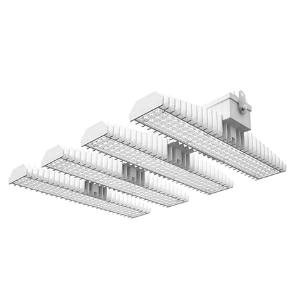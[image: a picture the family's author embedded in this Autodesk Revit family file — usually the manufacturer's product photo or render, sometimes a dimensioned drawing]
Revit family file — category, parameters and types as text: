
# Revit family: 3f_filippi_-_3f_lem_medio_3f_filippi_-_58895_a0811_-_3f_lem_4_led_200_cr_medio___vt_021e
name_source: partatom
category: Lighting Fixtures
units: mm (PartAtom-declared; Revit-internal decimal feet)

## family parameters
Cut with Voids When Loaded = No
Host = Face
Light Source = No
Part Type = Normal
Room Calculation Point = No
Round Connector Dimension = Use Diameter
Shared = No

## types (1)
- 3F Filippi - 3F LEM Medio (1 x LED, 30958 lm, 218 W, 4000 K)
    Apparent Load = 218 VA
    Approval mark = CE
    CIE Flux Codes = 83 96 99 100 100
    Color Rendering = 80
    Color Temperature = 4000 K
    Control Gear = Electronic ballast
    Default Elevation = 1800 mm
    Description = Industrial luminaire with high light output and high luminous efficiency designed with the most innovative technologies for environments with temperature up to 55°C.

ILLUMINOTECHNICAL
Luminous efficiency 100% (DLOR 99%, ULOR 1%).
Initial luminous flux of the luminaire 30958 lm.
Medium distribution with rectangular shape.
Installation Interdistance Transv.D = 1.02 x hu - Long.D = 1.06 x hu.
Tabular UGR (CIE 117 - 4H-8H; S=0.25H; 70/50/20): RUG 18.9 - 18.5.
Beam angle: 65° - 67°.
Luminous efficacy 142 lm/W.
Lifetime (L93/B10): 30000 h. (tq+25°C)
Lifetime (L90/B10): 50000 h. (tq+25°C)
Lifetime (L85/B10): 80000 h. (tq+25°C)
Lifetime (L80/B10): 100000 h. (tq+25°C)
Lifetime (L85/B10): 50000 h. (tq+55°C)
Sudden decreased luminous flux after 50000 hours: 0% (C0).
Photobiological safety in compliance with IEC/TR 62778: RG0 risk exempt, (IEC 62471).
In compliance with IEC/EN 62722-2-1 - IEC/EN 62717 standards.

SOURCE
4 Mid-Power linear LED modules 50W/840.
Energy efficiency class (UE 2019/2020 - UE 2019/2015): C.
CIE 13.3 Colour rendering index: CRI >80 (R9 <50%).
IES TM-30 Fidelity Index: Rf = 84 Rg = 95.
CCT nominal colour temperature 4000 K.
Colour initial tolerance (MacAdam): SDCM 3.

MECHANICAL
Passive modular heatsinks in die-casted aluminium, painted in white colour.
To optimize the thermal management of the LED module, the heatsinks are oversized and provided with self-cleaning of cooling fins.
Wiring body in aluminium and galvanised steel anchored solidly to the sinks and thermally separated.
3F Lens lenses with high luminous efficiency, transparent methacrylate (PMMA), fixed to the LED modules.
Fixing brackets in stainless steel.
Luminaire with limited surface temperature. - D - (EN 60598-2-24)
Dimensions: 757x542 mm, height 133 mm. Weight 18.688 kg.
IP65 protection degree.
Mechanical strength to impacts IK06 (1 joule).
Glow-wire test resistance 650°C.

ELECTRICAL
Halogen Free electronic wiring 230V-50/60Hz, power factor 0.97, THD <25%, constant output current, class I, 2 driver.
Power of the luminaire 218 W.
ENEC - CE.
SAFE FLICKER: PstLM=<1 and SVM=<0.4 (IEC TR 61547-1 and IEC TR 63158), to ensure a more comfortable and safe light.
Luminaire compliant with EN 60598-2-22 for power supply from a centralised emergency system CPSS (Central Power Supply System), not incorporated in the luminaire - high risk areas excluded. The default power and flux are 100% in AC and 100% in DC.
Ambient temperature from -30°C to +55°C.
Temperature class T6 max 85°C.
Quick connection via M20 3P connector with 9-13 mm tightening range.
Power unit positioned on a separate compartment by the LED module to ensure optimum temperatures of cabling components, to be inspectable and maintainable.
Relative humidity UR: <85%.

INSTALLATION
Ceiling / Suspended / Wall.
All accessories dedicated to this product are available on the Catalog and on our website www.3F-Filippi.com.

ACCESSORIES
A0811 - VT transparent glass, tempered, not flammable, with sealing gasket.
One required for each light module. The pack contains 10 pieces.

APPLICATIONS
In commercial environments, exhibition and industrial areas, stores, open areas.
Applications with high ambient temperature up to 55°C.
Environments in which it is necessary a total protection against falling fragments (eg environments with foodstuffs or machines with moving parts or with extreme temperature changes), use luminaires with polycarbonate lenses.

WARNING
Fixture not suitable for cold stores with an ambient temperature <0°C and/or relative humidity >85%.
Luminaire designed for disposal/recycling at end-of-life.
Replaceable (LED only) light source by a professional. Replaceable control gear by a professional.
    Height = 133 mm  [stored 0.436352 ft]
    Lamp = 1 x LED
    Lamp Light Flux = 30958 lm
    Lamp Power = 218 W
    Lamp count = 1
    Length = 757 mm
    Lifetime = 50000 h
    Luminous efficacy = 142 lm/W
    Manufacturer = 3F Filippi
    ModVariant = No
    Model = 3F Filippi - 58895+A0811 - 3F LEM 4 LED 200 CR MEDIO + VT
    Mounting Place = Ceiling
    Mounting Type = Pendant
    Number of Poles = 1
    OnlyDefault = Yes
    Power Factor = 1
    Product Name = 3F Filippi - 3F LEM Medio
    Product group = pendant luminaire
    ProductGroupID = 9
    Protection Class = Protection class I
    Protection Degree = IP 65
    RLX_Detail_Level = 1
    RLX_Emergency_Light_Flux = 0 lm
    RLX_Emergency_Type = 0
    RLX_Emergency_Type_DB = No
    RlxData = <blob elided: 118309 chars, md5=e3a0cee1>
    Socket = socket
    Standby Power = 0 W
    System Light Flux = 30958 lm
    System Power = 218 W
    Type Comments = Product without accessories
    Type Image = 3f_filippi_-_lem_4__a0811.jpg
    URL = http://relux.com
    VarID = ---
    Voltage = 0 V
    Weight = 0.00 kg
    Width = 542 mm

note: [stored X ft] marks values corroborated as IEEE doubles in the binary element streams (Revit-internal decimal feet)

## geometry (parser evidence)
native form markers: Blend x4, Sweep x13
no freeform markers — native parametric forms only
